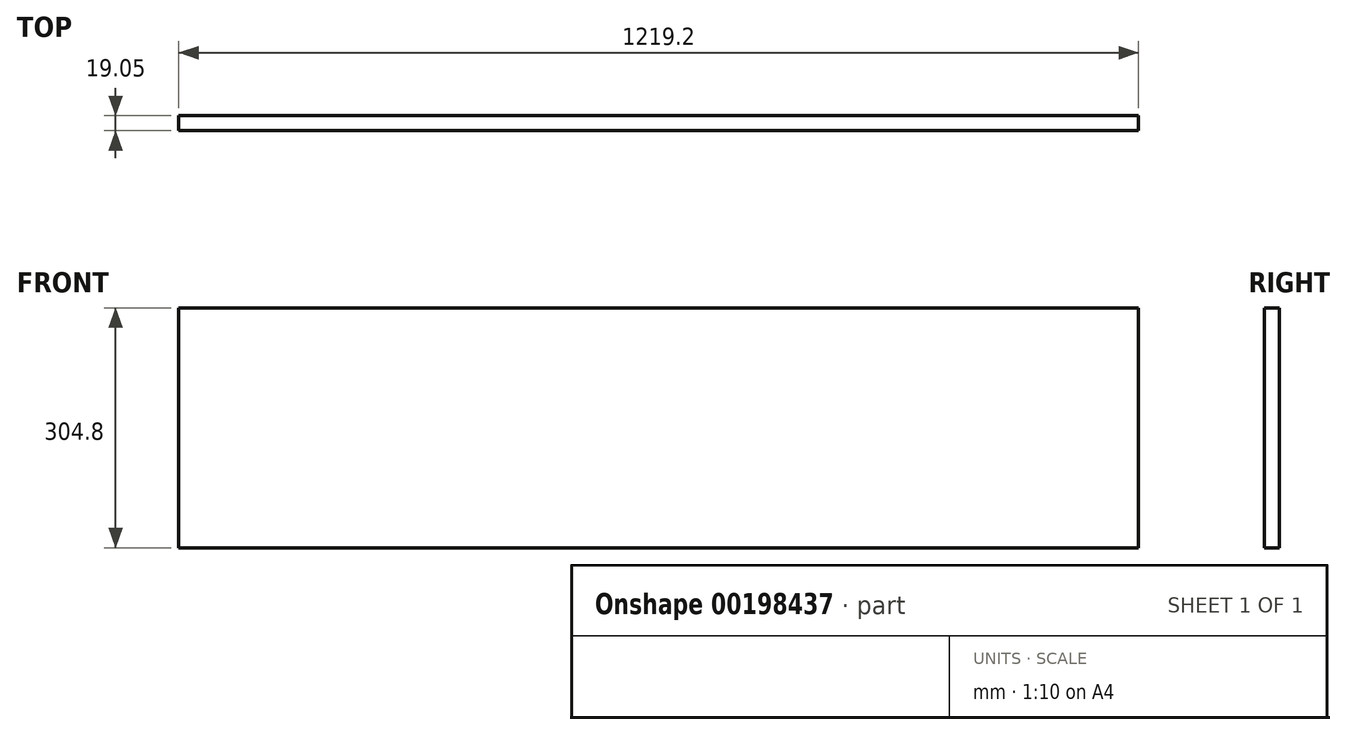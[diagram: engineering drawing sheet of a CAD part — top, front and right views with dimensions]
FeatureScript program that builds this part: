
annotation { "Feature Type Name" : "Feature", "Feature Type Description" : "" }
export const myFeature = defineFeature(function(context is Context, id is Id, definition is map)
    precondition{}
    {
        {
            var Q0;
            Q0=qCreatedBy(makeId("Front.planeOp"),FACE);
            var sketch = newSketch(context, id + "F0", { "sketchPlane" : qUnion([Q0])});
            skLineSegment(sketch, "E0.bottom", {"start": v(-609.6, 152.4) * mm, "end": v(609.6, 152.4) * mm});
            skLineSegment(sketch, "E0.top", {"start": v(-609.6, -152.4) * mm, "end": v(609.6, -152.4) * mm});
            skLineSegment(sketch, "E0.left", {"start": v(-609.6, 152.4) * mm, "end": v(-609.6, -152.4) * mm});
            skLineSegment(sketch, "E0.right", {"start": v(609.6, 152.4) * mm, "end": v(609.6, -152.4) * mm});
            skPoint(sketch, "E0.middle", {"position": v(0, 0) * mm});
            skSolve(sketch);
        }
        {
            var Q0;
            Q0 = qSketchRegion(id + "F0", true);
            extrude(context, id + "F1", {"entities" : qUnion([Q0]), "depth" : 19.05 * mm});
        }
    });
